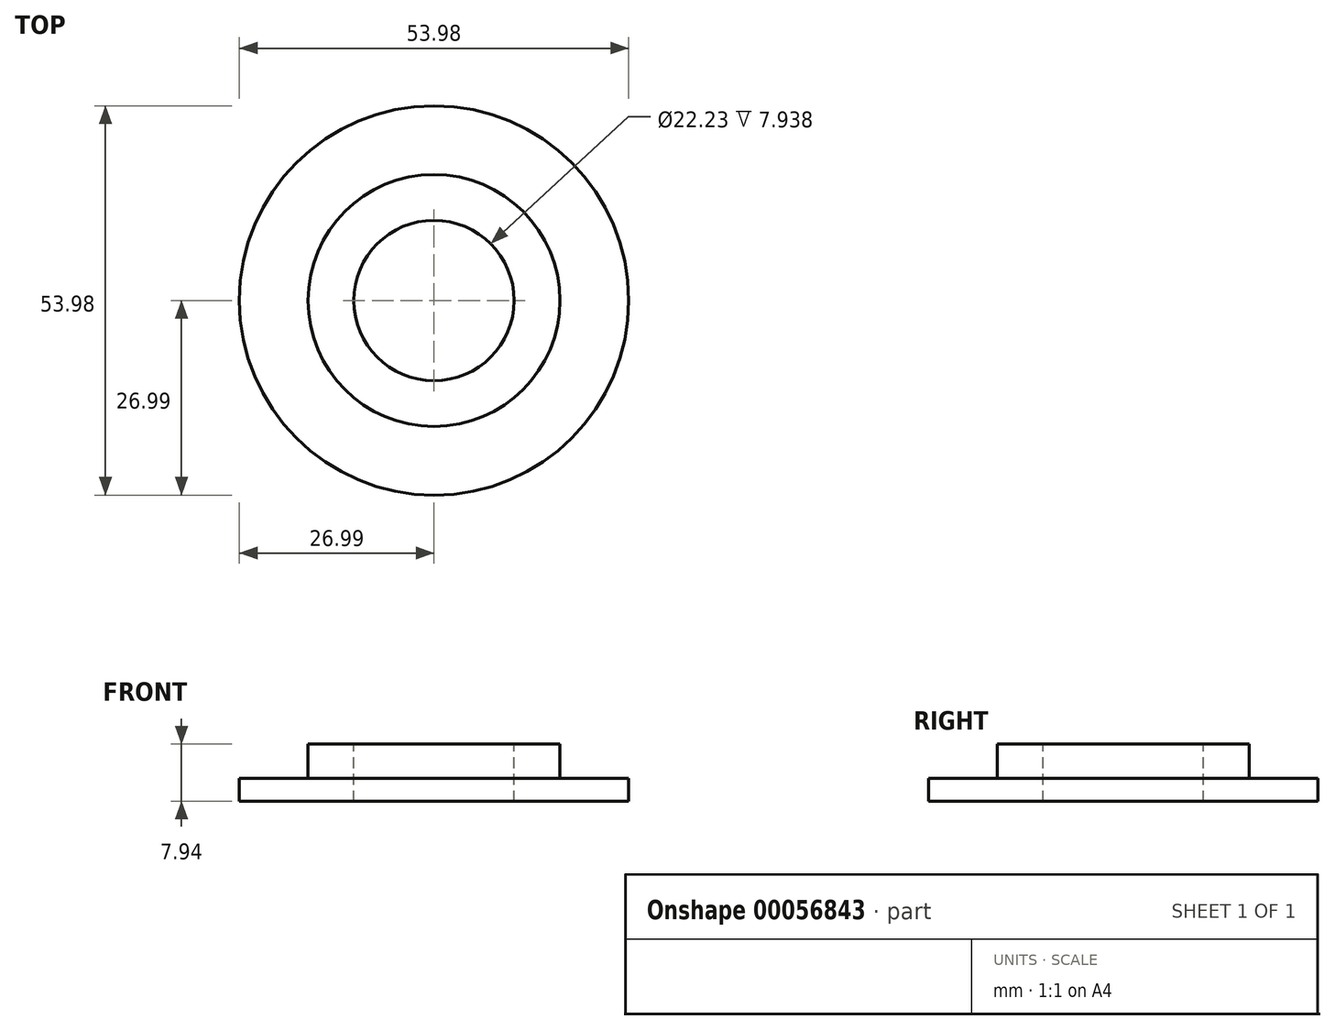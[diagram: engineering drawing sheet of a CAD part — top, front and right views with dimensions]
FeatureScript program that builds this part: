
annotation { "Feature Type Name" : "Feature", "Feature Type Description" : "" }
export const myFeature = defineFeature(function(context is Context, id is Id, definition is map)
    precondition{}
    {
        {
            var Q0;
            Q0=qCreatedBy(makeId("Top.planeOp"),FACE);
            var sketch = newSketch(context, id + "F0", { "sketchPlane" : qUnion([Q0])});
            skCircle(sketch, "E0", {"center": v(0, 0) * mm, "radius": 26.99 * mm});
            skSolve(sketch);
        }
        {
            var Q0;
            Q0 = qSketchRegion(id + "F0", true);
            extrude(context, id + "F1", {"entities" : qUnion([Q0]), "depth" : 3.17 * mm});
        }
        {
            var Q0;
            Q0=makeQuery(id+"F1.opExtrude","CAP_FACE",FACE,{"disambiguationData":[OSD([sQuery(id+"F0.wireOp",EDGE,"E0")])],"isStart":false});
            var sketch = newSketch(context, id + "F2", { "sketchPlane" : qUnion([Q0])});
            skCircle(sketch, "E1", {"center": v(0, 0) * mm, "radius": 17.46 * mm});
            skSolve(sketch);
        }
        {
            var Q0;
            Q0 = qSketchRegion(id + "F2", true);
            extrude(context, id + "F3", {"entities" : qUnion([Q0]), "operationType" : NewBodyOperationType.ADD, "depth" : 4.76 * mm});
        }
        {
            var Q0;
            Q0=makeQuery(id+"F3.opExtrude","CAP_FACE",FACE,{"disambiguationData":[OSD([sQuery(id+"F2.wireOp",EDGE,"E1")])],"isStart":false});
            var sketch = newSketch(context, id + "F4", { "sketchPlane" : qUnion([Q0])});
            skPoint(sketch, "E2", {"position": v(0, 0) * mm});
            skSolve(sketch);
        }
        {
            var Q0;
            Q0=sQuery(id+"F4.wireOp",VERTEX,"E2");
            var Q1;
            Q1=makeQuery(id+"F1.opExtrude","SWEPT_BODY",BODY,{"disambiguationData":[OSD([sQuery(id+"F0.wireOp",EDGE,"E0")])]});
            hole(context, id + "F5", {"style" : HoleStyle.SIMPLE, "holeDiameter" : 22.22 * mm, "endStyle" : HoleEndStyle.THROUGH, "locations" : qUnion([Q0]), "scope" : qUnion([Q1])});
        }
    });
